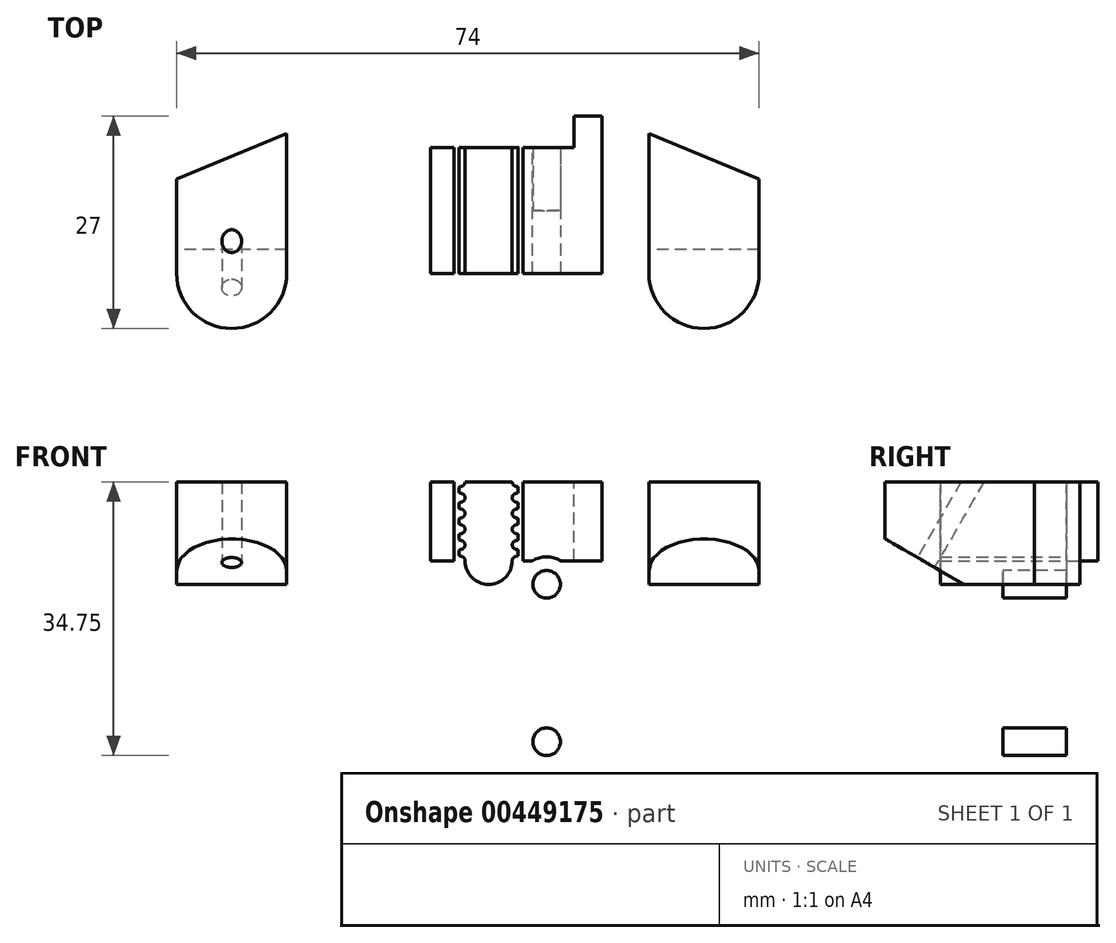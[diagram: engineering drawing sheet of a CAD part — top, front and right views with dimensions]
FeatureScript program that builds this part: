
annotation { "Feature Type Name" : "Feature", "Feature Type Description" : "" }
export const myFeature = defineFeature(function(context is Context, id is Id, definition is map)
    precondition{}
    {
        {
            var Q0;
            Q0=qCreatedBy(makeId("Top.planeOp"),FACE);
            var sketch = newSketch(context, id + "F0", { "sketchPlane" : qUnion([Q0])});
            skLineSegment(sketch, "E0", {"start": v(-30, 0) * mm, "end": v(30, 0) * mm, "construction": true});
            skLineSegment(sketch, "E1", {"start": v(-30, 0) * mm, "end": v(-30, -8) * mm, "construction": true});
            skArc(sketch, "E2", {"start": v(-37, -8) * mm, "mid": v(-30, -15) * mm, "end": v(-23, -8) * mm});
            skLineSegment(sketch, "E3", {"start": v(-30, -8) * mm, "end": v(-23, -8) * mm, "construction": true});
            skLineSegment(sketch, "E4", {"start": v(-30, -8) * mm, "end": v(-37, -8) * mm, "construction": true});
            skLineSegment(sketch, "E5", {"start": v(-23, -8) * mm, "end": v(-23, 0) * mm});
            skLineSegment(sketch, "E6", {"start": v(-23, 0) * mm, "end": v(0, 0) * mm});
            skLineSegment(sketch, "E7", {"start": v(-37, -8) * mm, "end": v(-37, 0) * mm});
            skLineSegment(sketch, "E8", {"start": v(-37, 0) * mm, "end": v(-37, 4) * mm});
            skLineSegment(sketch, "E9", {"start": v(0, 0) * mm, "end": v(0, 8) * mm, "construction": true});
            skLineSegment(sketch, "E10", {"start": v(-13.5, 8) * mm, "end": v(13.5, 8) * mm});
            skLineSegment(sketch, "E11", {"start": v(-13.5, 8) * mm, "end": v(-13.5, 12) * mm});
            skLineSegment(sketch, "E12", {"start": v(-13.5, 12) * mm, "end": v(-17.5, 12) * mm});
            skLineSegment(sketch, "E13", {"start": v(-37, 4) * mm, "end": v(-17.5, 12) * mm});
            skLineSegment(sketch, "E14.MirrorCS", {"start": v(23, -8) * mm, "end": v(23, 0) * mm});
            skArc(sketch, "E15.MirrorCS", {"start": v(37, -8) * mm, "mid": v(30, -15) * mm, "end": v(23, -8) * mm});
            skLineSegment(sketch, "E16.MirrorCS", {"start": v(37, -8) * mm, "end": v(37, 0) * mm});
            skLineSegment(sketch, "E17.MirrorCS", {"start": v(37, 0) * mm, "end": v(37, 4) * mm});
            skLineSegment(sketch, "E18.MirrorCS", {"start": v(37, 4) * mm, "end": v(17.5, 12) * mm});
            skLineSegment(sketch, "E19.MirrorCS", {"start": v(13.5, 12) * mm, "end": v(17.5, 12) * mm});
            skLineSegment(sketch, "E20.MirrorCS", {"start": v(13.5, 8) * mm, "end": v(13.5, 12) * mm});
            skLineSegment(sketch, "E21", {"start": v(0, 0) * mm, "end": v(23, 0) * mm});
            skLineSegment(sketch, "E22", {"start": v(-17.5, 12) * mm, "end": v(-17.5, 0) * mm});
            skLineSegment(sketch, "E23.MirrorCS", {"start": v(17.5, 12) * mm, "end": v(17.5, 0) * mm});
            skSolve(sketch);
        }
        {
            var Q0;
            Q0=makeQuery(id+"F0.imprint","IMPRINT",FACE,{"disambiguationData":[TD([[makeQuery(id+"F0.imprint","IMPRINT",EDGE,{"derivedFrom":sQuery(id+"F0.wireOp",EDGE,"E10")}),-1.0]])]});
            extrude(context, id + "F1", {"entities" : qUnion([Q0]), "oppositeDirection" : true, "depth" : 50 * mm});
        }
        {
            var Q0;
            Q0=makeQuery(id+"F0.imprint","IMPRINT",FACE,{"disambiguationData":[TD([[makeQuery(id+"F0.imprint","IMPRINT",EDGE,{"derivedFrom":sQuery(id+"F0.wireOp",EDGE,"E2")}),1.0]])]});
            var Q1;
            {var subQ0=sQuery(id+"F0.wireOp",EDGE,"E14.MirrorCS");Q1=makeQuery(id+"F0.imprint","IMPRINT",FACE,{"disambiguationData":[TD([[makeQuery(id+"F0.imprint","IMPRINT",EDGE,{"derivedFrom":subQ0}),-1.0]])]});}
            extrude(context, id + "F2", {"entities" : qUnion([Q0, Q1]), "operationType" : NewBodyOperationType.ADD, "oppositeDirection" : true, "depth" : 13 * mm});
        }
        {
            var Q0;
            Q0=makeQuery(id+"F2.opExtrude","SWEPT_FACE",FACE,{"disambiguationData":[OSD([sQuery(id+"F0.wireOp",EDGE,"E7"),sQuery(id+"F0.wireOp",EDGE,"E8")])]});
            var sketch = newSketch(context, id + "F3", { "sketchPlane" : qUnion([Q0])});
            skPoint(sketch, "E24.0", {"position": v(8, -13) * mm});
            skLineSegment(sketch, "E25", {"start": v(8, -13) * mm, "end": v(5, -13) * mm});
            skLineSegment(sketch, "E26", {"start": v(15, 0) * mm, "end": v(15, -13) * mm, "construction": true});
            skLineSegment(sketch, "E27", {"start": v(5, -13) * mm, "end": v(15, -7.23) * mm});
            skLineSegment(sketch, "E28", {"start": v(8, -13) * mm, "end": v(15, -13) * mm});
            skLineSegment(sketch, "E29", {"start": v(15, -7.23) * mm, "end": v(15, -13) * mm});
            skSolve(sketch);
        }
        {
            var Q0;
            {var subQ4=sQuery(id+"F3.wireOp",EDGE,"E28");Q0=makeQuery(id+"F3.imprint","IMPRINT",FACE,{"disambiguationData":[TD([[makeQuery(id+"F3.imprint","IMPRINT",EDGE,{"derivedFrom":subQ4}),1.0]])]});}
            var Q1;
            {var subQ0=sQuery(id+"F3.wireOp",EDGE,"E25");Q1=makeQuery(id+"F3.imprint","IMPRINT",FACE,{"disambiguationData":[TD([[makeQuery(id+"F3.imprint","IMPRINT",EDGE,{"derivedFrom":subQ0}),-1.0]])]});}
            extrude(context, id + "F4", {"entities" : qUnion([Q0, Q1]), "operationType" : NewBodyOperationType.REMOVE, "endBound" : BoundingType.THROUGH_ALL, "oppositeDirection" : true, "depth" : 25 * mm});
        }
        {
            var Q0;
            {var subQ0=sQuery(id+"F0.wireOp",EDGE,"E2");Q0=makeQuery(id+"F4.boolean.opBoolean","COPY",FACE,{"disambiguationData":[TD([makeQuery(id+"F2.opExtrude","SWEPT_FACE",FACE,{"disambiguationData":[OSD([subQ0])]})])],"derivedFrom":makeQuery(id+"F4.opExtrude","SWEPT_FACE",FACE,{"disambiguationData":[OSD([sQuery(id+"F3.wireOp",EDGE,"E27")])]})});}
            var sketch = newSketch(context, id + "F5", { "sketchPlane" : qUnion([Q0])});
            skPoint(sketch, "E30.0", {"position": v(0, 0) * mm});
            skPoint(sketch, "E31.0", {"position": v(-30, 9.38) * mm});
            skLineSegment(sketch, "E32", {"start": v(-30, 9.38) * mm, "end": v(-30, 3.38) * mm, "construction": true});
            skCircle(sketch, "E33", {"center": v(-30, 3.38) * mm, "radius": 1.25 * mm});
            skLineSegment(sketch, "E34", {"start": v(0, 0) * mm, "end": v(0, -5.42) * mm, "construction": true});
            skCircle(sketch, "E35.MirrorC", {"center": v(30, 3.38) * mm, "radius": 1.25 * mm});
            skSolve(sketch);
        }
        {
            var Q0;
            Q0=makeQuery(id+"F5.imprint","IMPRINT",FACE,{"disambiguationData":[TD([[makeQuery(id+"F5.imprint","IMPRINT",EDGE,{"derivedFrom":sQuery(id+"F5.wireOp",EDGE,"E33")}),1.0]])]});
            var Q1;
            Q1=makeQuery(id+"F5.imprint","IMPRINT",FACE,{"disambiguationData":[TD([[makeQuery(id+"F5.imprint","IMPRINT",EDGE,{"derivedFrom":sQuery(id+"F5.wireOp",EDGE,"E35.MirrorC")}),-1.0]])]});
            extrude(context, id + "F6", {"entities" : qUnion([Q0, Q1]), "operationType" : NewBodyOperationType.REMOVE, "oppositeDirection" : true, "depth" : 15 * mm});
        }
        {
            var Q0;
            {var subQ0=sQuery(id+"F0.wireOp",EDGE,"E21");var subQ1=sQuery(id+"F0.wireOp",EDGE,"E6");Q0=makeQuery(id+"F2.boolean.opBoolean","MERGE",FACE,{"derivedFrom":[makeQuery(id+"F1.opExtrude","SWEPT_FACE",FACE,{"disambiguationData":[OSD([subQ1,subQ0])]}),makeQuery(id+"F2.opExtrude","SWEPT_FACE",FACE,{"disambiguationData":[OSD([subQ1])]}),makeQuery(id+"F2.opExtrude","SWEPT_FACE",FACE,{"disambiguationData":[OSD([subQ0])]})]});}
            var sketch = newSketch(context, id + "F7", { "sketchPlane" : qUnion([Q0])});
            skLineSegment(sketch, "E36", {"start": v(0, 0) * mm, "end": v(0, -13) * mm, "construction": true});
            skLineSegment(sketch, "E37", {"start": v(0, -13) * mm, "end": v(-10, -13) * mm, "construction": true});
            skLineSegment(sketch, "E38", {"start": v(-10, -13) * mm, "end": v(-10, -33) * mm, "construction": true});
            skCircle(sketch, "E39", {"center": v(-10, -13) * mm, "radius": 1.75 * mm});
            skCircle(sketch, "E40", {"center": v(-10, -33) * mm, "radius": 1.75 * mm});
            skCircle(sketch, "E41.MirrorC", {"center": v(10, -13) * mm, "radius": 1.75 * mm});
            skCircle(sketch, "E42.MirrorC", {"center": v(10, -33) * mm, "radius": 1.75 * mm});
            skPoint(sketch, "E43", {"position": v(5.64, 0) * mm});
            skPoint(sketch, "E44", {"position": v(7.03, 0) * mm});
            skLineSegment(sketch, "E45.0", {"start": v(6.39, -1) * mm, "end": v(6.39, -1.26) * mm});
            skArc(sketch, "E46", {"start": v(5.95, -1.5) * mm, "mid": v(5.72, -1.7) * mm, "end": v(5.64, -2) * mm});
            skArc(sketch, "E47", {"start": v(6.26, -1.4) * mm, "mid": v(6.1, -1.44) * mm, "end": v(5.95, -1.5) * mm});
            skArc(sketch, "E48.filletArc", {"start": v(6.26, -1.4) * mm, "mid": v(6.35, -1.36) * mm, "end": v(6.4, -1.26) * mm});
            skLineSegment(sketch, "E49.MirrorCS", {"start": v(6.39, -1) * mm, "end": v(6.39, -0.74) * mm});
            skArc(sketch, "E50.MirrorCS", {"start": v(6.26, -0.6) * mm, "mid": v(6.35, -0.64) * mm, "end": v(6.4, -0.74) * mm});
            skArc(sketch, "E51.MirrorCS", {"start": v(6.26, -0.6) * mm, "mid": v(6.1, -0.56) * mm, "end": v(5.95, -0.5) * mm});
            skArc(sketch, "E52.MirrorCS", {"start": v(5.95, -0.5) * mm, "mid": v(5.72, -0.3) * mm, "end": v(5.64, 0) * mm});
            skArc(sketch, "E53.0.1.0", {"start": v(5.95, -3.5) * mm, "mid": v(5.72, -3.7) * mm, "end": v(5.64, -4) * mm});
            skPoint(sketch, "E53.0.1.1", {"position": v(5.64, -2) * mm});
            skLineSegment(sketch, "E53.0.1.2", {"start": v(6.39, -3) * mm, "end": v(6.39, -3.26) * mm});
            skArc(sketch, "E53.0.1.3", {"start": v(6.26, -3.4) * mm, "mid": v(6.1, -3.44) * mm, "end": v(5.95, -3.5) * mm});
            skLineSegment(sketch, "E53.0.1.4", {"start": v(6.39, -3) * mm, "end": v(6.39, -2.74) * mm});
            skArc(sketch, "E53.0.1.5", {"start": v(6.26, -2.6) * mm, "mid": v(6.35, -2.64) * mm, "end": v(6.4, -2.74) * mm});
            skArc(sketch, "E53.0.1.6", {"start": v(6.26, -2.6) * mm, "mid": v(6.1, -2.56) * mm, "end": v(5.95, -2.5) * mm});
            skArc(sketch, "E53.0.1.7", {"start": v(6.26, -3.4) * mm, "mid": v(6.35, -3.36) * mm, "end": v(6.4, -3.26) * mm});
            skArc(sketch, "E53.0.1.8", {"start": v(5.95, -2.5) * mm, "mid": v(5.72, -2.3) * mm, "end": v(5.64, -2) * mm});
            skArc(sketch, "E53.0.2.0", {"start": v(5.95, -5.5) * mm, "mid": v(5.72, -5.7) * mm, "end": v(5.64, -6) * mm});
            skPoint(sketch, "E53.0.2.1", {"position": v(5.64, -4) * mm});
            skLineSegment(sketch, "E53.0.2.2", {"start": v(6.39, -5) * mm, "end": v(6.39, -5.26) * mm});
            skArc(sketch, "E53.0.2.3", {"start": v(6.26, -5.4) * mm, "mid": v(6.1, -5.44) * mm, "end": v(5.95, -5.5) * mm});
            skLineSegment(sketch, "E53.0.2.4", {"start": v(6.39, -5) * mm, "end": v(6.39, -4.74) * mm});
            skArc(sketch, "E53.0.2.5", {"start": v(6.26, -4.6) * mm, "mid": v(6.35, -4.64) * mm, "end": v(6.4, -4.74) * mm});
            skArc(sketch, "E53.0.2.6", {"start": v(6.26, -4.6) * mm, "mid": v(6.1, -4.56) * mm, "end": v(5.95, -4.5) * mm});
            skArc(sketch, "E53.0.2.7", {"start": v(6.26, -5.4) * mm, "mid": v(6.35, -5.36) * mm, "end": v(6.4, -5.26) * mm});
            skArc(sketch, "E53.0.2.8", {"start": v(5.95, -4.5) * mm, "mid": v(5.72, -4.3) * mm, "end": v(5.64, -4) * mm});
            skLineSegment(sketch, "E53.direction1", {"start": v(5.64, -2) * mm, "end": v(30.64, -2) * mm, "construction": true});
            skLineSegment(sketch, "E53.direction2", {"start": v(5.64, -2) * mm, "end": v(5.64, -4) * mm, "construction": true});
            skArc(sketch, "E54.0.0.3", {"start": v(5.95, -7.5) * mm, "mid": v(5.72, -7.7) * mm, "end": v(5.64, -8) * mm});
            skPoint(sketch, "E54.4.0.3", {"position": v(5.64, -6) * mm});
            skLineSegment(sketch, "E54.5.0.3", {"start": v(6.39, -7) * mm, "end": v(6.39, -7.26) * mm});
            skArc(sketch, "E54.8.0.3", {"start": v(6.26, -7.4) * mm, "mid": v(6.1, -7.44) * mm, "end": v(5.95, -7.5) * mm});
            skLineSegment(sketch, "E54.12.0.3", {"start": v(6.39, -7) * mm, "end": v(6.39, -6.74) * mm});
            skArc(sketch, "E54.15.0.3", {"start": v(6.26, -6.6) * mm, "mid": v(6.35, -6.64) * mm, "end": v(6.4, -6.74) * mm});
            skArc(sketch, "E54.19.0.3", {"start": v(6.26, -6.6) * mm, "mid": v(6.1, -6.56) * mm, "end": v(5.95, -6.5) * mm});
            skArc(sketch, "E54.23.0.3", {"start": v(6.26, -7.4) * mm, "mid": v(6.35, -7.36) * mm, "end": v(6.4, -7.26) * mm});
            skArc(sketch, "E54.27.0.3", {"start": v(5.95, -6.5) * mm, "mid": v(5.72, -6.3) * mm, "end": v(5.64, -6) * mm});
            skArc(sketch, "E55.0.0.4", {"start": v(5.95, -9.5) * mm, "mid": v(5.72, -9.7) * mm, "end": v(5.64, -10) * mm});
            skPoint(sketch, "E55.4.0.4", {"position": v(5.64, -8) * mm});
            skLineSegment(sketch, "E55.5.0.4", {"start": v(6.39, -9) * mm, "end": v(6.39, -9.26) * mm});
            skArc(sketch, "E55.8.0.4", {"start": v(6.26, -9.4) * mm, "mid": v(6.1, -9.44) * mm, "end": v(5.95, -9.5) * mm});
            skLineSegment(sketch, "E55.12.0.4", {"start": v(6.39, -9) * mm, "end": v(6.39, -8.74) * mm});
            skArc(sketch, "E55.15.0.4", {"start": v(6.26, -8.6) * mm, "mid": v(6.35, -8.64) * mm, "end": v(6.4, -8.74) * mm});
            skArc(sketch, "E55.19.0.4", {"start": v(6.26, -8.6) * mm, "mid": v(6.1, -8.56) * mm, "end": v(5.95, -8.5) * mm});
            skArc(sketch, "E55.23.0.4", {"start": v(6.26, -9.4) * mm, "mid": v(6.35, -9.36) * mm, "end": v(6.4, -9.26) * mm});
            skArc(sketch, "E55.27.0.4", {"start": v(5.95, -8.5) * mm, "mid": v(5.72, -8.3) * mm, "end": v(5.64, -8) * mm});
            skLineSegment(sketch, "E56", {"start": v(7.03, 0) * mm, "end": v(7.03, -10) * mm});
            skLineSegment(sketch, "E57", {"start": v(7.03, -10) * mm, "end": v(8.2, -10) * mm});
            skLineSegment(sketch, "E58", {"start": v(17.03, -10) * mm, "end": v(17.03, 0) * mm});
            skLineSegment(sketch, "E59", {"start": v(17.03, 0) * mm, "end": v(7.03, 0) * mm});
            skLineSegment(sketch, "E60", {"start": v(5.64, -10) * mm, "end": v(2.64, -10) * mm, "construction": true});
            skArc(sketch, "E61", {"start": v(-0.36, -10) * mm, "mid": v(2.64, -13) * mm, "end": v(5.64, -10) * mm});
            skLineSegment(sketch, "E62", {"start": v(2.64, -10) * mm, "end": v(-0.36, -10) * mm, "construction": true});
            skLineSegment(sketch, "E63", {"start": v(2.64, -10) * mm, "end": v(2.64, -8.7) * mm, "construction": true});
            skArc(sketch, "E64.MirrorCS", {"start": v(-0.98, -2.6) * mm, "mid": v(-1.07, -2.64) * mm, "end": v(-1.11, -2.74) * mm});
            skLineSegment(sketch, "E65.MirrorCS", {"start": v(-1.11, -3) * mm, "end": v(-1.11, -2.74) * mm});
            skArc(sketch, "E66.MirrorCS", {"start": v(-0.98, -4.6) * mm, "mid": v(-1.07, -4.64) * mm, "end": v(-1.11, -4.74) * mm});
            skLineSegment(sketch, "E67.MirrorCS", {"start": v(-1.11, -3) * mm, "end": v(-1.11, -3.26) * mm});
            skLineSegment(sketch, "E68.MirrorCS", {"start": v(-1.11, -5) * mm, "end": v(-1.11, -4.74) * mm});
            skArc(sketch, "E69.MirrorCS", {"start": v(-0.98, -3.4) * mm, "mid": v(-1.07, -3.36) * mm, "end": v(-1.11, -3.26) * mm});
            skArc(sketch, "E70.MirrorCS", {"start": v(-0.98, -5.4) * mm, "mid": v(-1.07, -5.36) * mm, "end": v(-1.11, -5.26) * mm});
            skLineSegment(sketch, "E71.MirrorCS", {"start": v(-1.11, -1) * mm, "end": v(-1.11, -0.74) * mm});
            skLineSegment(sketch, "E72.MirrorCS", {"start": v(-1.11, -5) * mm, "end": v(-1.11, -5.26) * mm});
            skArc(sketch, "E73.MirrorCS", {"start": v(-0.98, -9.4) * mm, "mid": v(-1.07, -9.36) * mm, "end": v(-1.11, -9.26) * mm});
            skLineSegment(sketch, "E74.MirrorCS", {"start": v(-1.11, -7) * mm, "end": v(-1.11, -7.26) * mm});
            skLineSegment(sketch, "E75.MirrorCS", {"start": v(-1.11, -9) * mm, "end": v(-1.11, -9.26) * mm});
            skArc(sketch, "E76.MirrorCS", {"start": v(-0.98, -7.4) * mm, "mid": v(-1.07, -7.36) * mm, "end": v(-1.11, -7.26) * mm});
            skLineSegment(sketch, "E77.MirrorCS", {"start": v(-1.11, -1) * mm, "end": v(-1.11, -1.26) * mm});
            skArc(sketch, "E78.MirrorCS", {"start": v(-0.98, -0.6) * mm, "mid": v(-0.82, -0.56) * mm, "end": v(-0.67, -0.5) * mm});
            skArc(sketch, "E79.MirrorCS", {"start": v(-0.98, -6.6) * mm, "mid": v(-0.82, -6.56) * mm, "end": v(-0.67, -6.5) * mm});
            skArc(sketch, "E80.MirrorCS", {"start": v(-0.67, -2.5) * mm, "mid": v(-0.44, -2.3) * mm, "end": v(-0.36, -2) * mm});
            skArc(sketch, "E81.MirrorCS", {"start": v(-0.67, -8.5) * mm, "mid": v(-0.44, -8.3) * mm, "end": v(-0.36, -8) * mm});
            skArc(sketch, "E82.MirrorCS", {"start": v(-0.98, -2.6) * mm, "mid": v(-0.82, -2.56) * mm, "end": v(-0.67, -2.5) * mm});
            skArc(sketch, "E83.MirrorCS", {"start": v(-0.98, -4.6) * mm, "mid": v(-0.82, -4.56) * mm, "end": v(-0.67, -4.5) * mm});
            skLineSegment(sketch, "E84.MirrorCS", {"start": v(-1.11, -7) * mm, "end": v(-1.11, -6.74) * mm});
            skArc(sketch, "E85.MirrorCS", {"start": v(-0.98, -9.4) * mm, "mid": v(-0.82, -9.44) * mm, "end": v(-0.67, -9.5) * mm});
            skArc(sketch, "E86.MirrorCS", {"start": v(-0.98, -8.6) * mm, "mid": v(-1.07, -8.64) * mm, "end": v(-1.11, -8.74) * mm});
            skLineSegment(sketch, "E87.MirrorCS", {"start": v(-1.11, -9) * mm, "end": v(-1.11, -8.74) * mm});
            skArc(sketch, "E88.MirrorCS", {"start": v(-0.98, -0.6) * mm, "mid": v(-1.07, -0.64) * mm, "end": v(-1.11, -0.74) * mm});
            skArc(sketch, "E89.MirrorCS", {"start": v(-0.98, -1.4) * mm, "mid": v(-1.07, -1.36) * mm, "end": v(-1.11, -1.26) * mm});
            skArc(sketch, "E90.MirrorCS", {"start": v(-0.98, -7.4) * mm, "mid": v(-0.82, -7.44) * mm, "end": v(-0.67, -7.5) * mm});
            skArc(sketch, "E91.MirrorCS", {"start": v(-0.98, -3.4) * mm, "mid": v(-0.82, -3.44) * mm, "end": v(-0.67, -3.5) * mm});
            skArc(sketch, "E92.MirrorCS", {"start": v(-0.67, -7.5) * mm, "mid": v(-0.44, -7.7) * mm, "end": v(-0.36, -8) * mm});
            skArc(sketch, "E93.MirrorCS", {"start": v(-0.67, -5.5) * mm, "mid": v(-0.44, -5.7) * mm, "end": v(-0.36, -6) * mm});
            skArc(sketch, "E94.MirrorCS", {"start": v(-0.67, -0.5) * mm, "mid": v(-0.44, -0.3) * mm, "end": v(-0.36, 0) * mm});
            skArc(sketch, "E95.MirrorCS", {"start": v(-0.67, -3.5) * mm, "mid": v(-0.44, -3.7) * mm, "end": v(-0.36, -4) * mm});
            skArc(sketch, "E96.MirrorCS", {"start": v(-0.67, -6.5) * mm, "mid": v(-0.44, -6.3) * mm, "end": v(-0.36, -6) * mm});
            skArc(sketch, "E97.MirrorCS", {"start": v(-0.98, -1.4) * mm, "mid": v(-0.82, -1.44) * mm, "end": v(-0.67, -1.5) * mm});
            skArc(sketch, "E98.MirrorCS", {"start": v(-0.67, -1.5) * mm, "mid": v(-0.44, -1.7) * mm, "end": v(-0.36, -2) * mm});
            skArc(sketch, "E99.MirrorCS", {"start": v(-0.67, -4.5) * mm, "mid": v(-0.44, -4.3) * mm, "end": v(-0.36, -4) * mm});
            skArc(sketch, "E100.MirrorCS", {"start": v(-0.98, -5.4) * mm, "mid": v(-0.82, -5.44) * mm, "end": v(-0.67, -5.5) * mm});
            skArc(sketch, "E101.MirrorCS", {"start": v(-0.98, -6.6) * mm, "mid": v(-1.07, -6.64) * mm, "end": v(-1.11, -6.74) * mm});
            skArc(sketch, "E102.MirrorCS", {"start": v(-0.98, -8.6) * mm, "mid": v(-0.82, -8.56) * mm, "end": v(-0.67, -8.5) * mm});
            skPoint(sketch, "E103.MirrorP", {"position": v(-0.36, -8) * mm});
            skLineSegment(sketch, "E104.MirrorCS", {"start": v(-0.36, -2) * mm, "end": v(-0.36, -4) * mm, "construction": true});
            skPoint(sketch, "E105.MirrorP", {"position": v(-0.36, -2) * mm});
            skPoint(sketch, "E106.MirrorP", {"position": v(-0.36, -6) * mm});
            skPoint(sketch, "E107.MirrorP", {"position": v(-0.36, -4) * mm});
            skPoint(sketch, "E108.MirrorP", {"position": v(-0.36, 0) * mm});
            skPoint(sketch, "E109.MirrorP", {"position": v(-1.75, 0) * mm});
            skArc(sketch, "E110.MirrorCS", {"start": v(-0.67, -9.5) * mm, "mid": v(-0.44, -9.7) * mm, "end": v(-0.36, -10) * mm});
            skLineSegment(sketch, "E111", {"start": v(-0.36, 0) * mm, "end": v(5.64, 0) * mm});
            skArc(sketch, "E112", {"start": v(11.8, -10) * mm, "mid": v(10, -9.5) * mm, "end": v(8.2, -10) * mm});
            skLineSegment(sketch, "E113.trimOffspring", {"start": v(11.8, -10) * mm, "end": v(17.03, -10) * mm});
            skLineSegment(sketch, "E114", {"start": v(-1.75, 0) * mm, "end": v(-1.75, -10) * mm});
            skLineSegment(sketch, "E115.0", {"start": v(-4.75, 0) * mm, "end": v(-4.75, -10) * mm});
            skLineSegment(sketch, "E116", {"start": v(-4.75, -10) * mm, "end": v(-1.75, -10) * mm});
            skLineSegment(sketch, "E117", {"start": v(-4.75, 0) * mm, "end": v(-1.75, 0) * mm});
            skSolve(sketch);
        }
        {
            var Q0;
            Q0=makeQuery(id+"F7.imprint","IMPRINT",FACE,{"disambiguationData":[TD([[makeQuery(id+"F7.imprint","IMPRINT",EDGE,{"derivedFrom":sQuery(id+"F7.wireOp",EDGE,"E56")}),1.0]])]});
            var Q1;
            Q1=makeQuery(id+"F7.imprint","IMPRINT",FACE,{"disambiguationData":[TD([[makeQuery(id+"F7.imprint","IMPRINT",EDGE,{"derivedFrom":sQuery(id+"F7.wireOp",EDGE,"E45.0")}),-1.0]])]});
            var Q2;
            Q2=makeQuery(id+"F7.imprint","IMPRINT",FACE,{"disambiguationData":[TD([[makeQuery(id+"F7.imprint","IMPRINT",EDGE,{"derivedFrom":sQuery(id+"F7.wireOp",EDGE,"E114")}),-1.0]])]});
            extrude(context, id + "F8", {"entities" : qUnion([Q0, Q1, Q2]), "operationType" : NewBodyOperationType.ADD, "depth" : 8 * mm});
        }
        {
            var Q0;
            Q0=makeQuery(id+"F7.imprint","IMPRINT",FACE,{"disambiguationData":[TD([[makeQuery(id+"F7.imprint","IMPRINT",EDGE,{"derivedFrom":sQuery(id+"F7.wireOp",EDGE,"E39")}),1.0]])]});
            var Q1;
            Q1=makeQuery(id+"F7.imprint","IMPRINT",FACE,{"disambiguationData":[TD([[makeQuery(id+"F7.imprint","IMPRINT",EDGE,{"derivedFrom":sQuery(id+"F7.wireOp",EDGE,"E41.MirrorC")}),-1.0]])]});
            var Q2;
            Q2=makeQuery(id+"F7.imprint","IMPRINT",FACE,{"disambiguationData":[TD([[makeQuery(id+"F7.imprint","IMPRINT",EDGE,{"derivedFrom":sQuery(id+"F7.wireOp",EDGE,"E42.MirrorC")}),-1.0]])]});
            var Q3;
            Q3=makeQuery(id+"F7.imprint","IMPRINT",FACE,{"disambiguationData":[TD([[makeQuery(id+"F7.imprint","IMPRINT",EDGE,{"derivedFrom":sQuery(id+"F7.wireOp",EDGE,"E40")}),1.0]])]});
            extrude(context, id + "F9", {"entities" : qUnion([Q0, Q1, Q2, Q3]), "operationType" : NewBodyOperationType.REMOVE, "oppositeDirection" : true, "depth" : 25 * mm});
        }
    });
